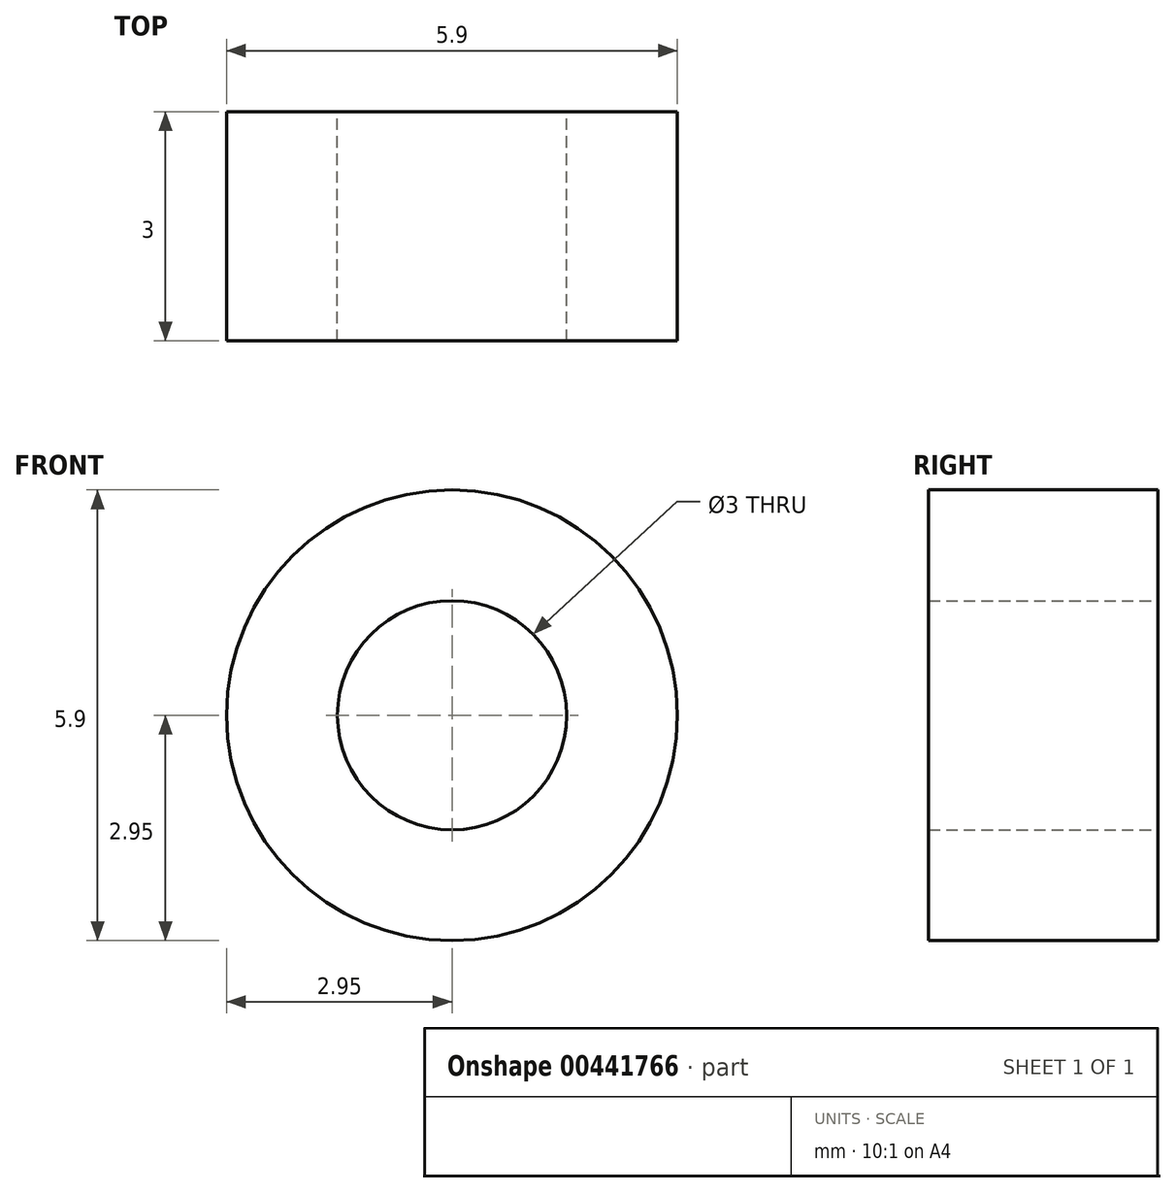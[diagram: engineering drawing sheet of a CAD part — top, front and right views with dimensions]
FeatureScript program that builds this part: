
annotation { "Feature Type Name" : "Feature", "Feature Type Description" : "" }
export const myFeature = defineFeature(function(context is Context, id is Id, definition is map)
    precondition{}
    {
        {
            var Q0;
            Q0=qCreatedBy(makeId("Front.planeOp"),FACE);
            var sketch = newSketch(context, id + "F0", { "sketchPlane" : qUnion([Q0])});
            skCircle(sketch, "E0", {"center": v(0, 0) * mm, "radius": 2.95 * mm});
            skCircle(sketch, "E1", {"center": v(0, 0) * mm, "radius": 1.5 * mm});
            skSolve(sketch);
        }
        {
            var Q0;
            Q0 = qSketchRegion(id + "F0", true);
            extrude(context, id + "F1", {"entities" : qUnion([Q0]), "depth" : 3 * mm});
        }
    });
